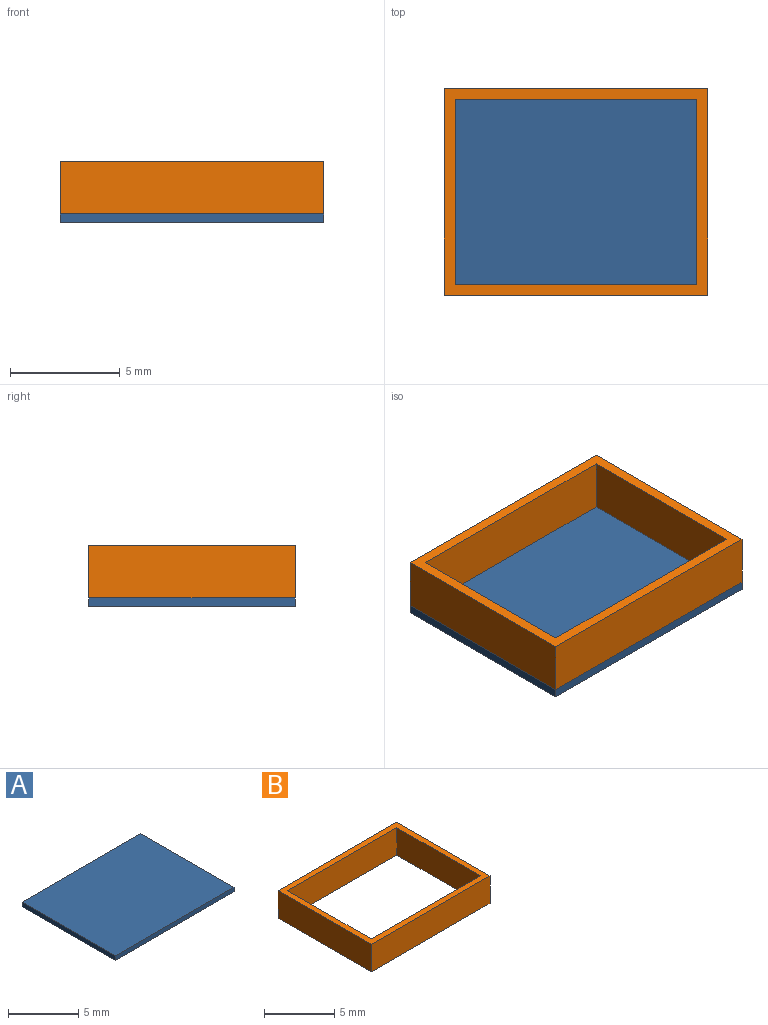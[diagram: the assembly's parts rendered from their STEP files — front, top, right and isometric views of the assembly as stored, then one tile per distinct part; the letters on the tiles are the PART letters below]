
ASSEMBLY  parts=2 mates=1
PART A: 6 faces, bbox 12x9.4x0.4 mm
  f0: plane 9.4x0.4mm, normal (-1,0,0), area 3.8mm2, adj f1,f3,f4,f5
  f1: plane 12x0.4mm, normal (0,-1,0), area 4.8mm2, adj f0,f2,f4,f5
  f2: plane 9.4x0.4mm, normal (1,0,0), area 3.8mm2, adj f1,f3,f4,f5
  f3: plane 12x0.4mm, normal (0,1,0), area 4.8mm2, adj f0,f2,f4,f5
  f4: plane 12x9.4mm, normal (0,0,-1), area 112.8mm2, adj f0,f1,f2,f3
  f5: plane 12x9.4mm, normal (0,0,1), area 112.8mm2, adj f0,f1,f2,f3
PART B: 10 faces, bbox 12x9.4x2.4 mm
  f0: plane 8.42x2.4mm, normal (-1,0,0), area 20.2mm2, adj f1,f7,f8,f9
  f1: plane 11.02x2.4mm, normal (0,1,0), area 26.4mm2, adj f0,f2,f8,f9
  f2: plane 8.42x2.4mm, normal (1,0,0), area 20.2mm2, adj f1,f7,f8,f9
  f3: plane 9.4x2.4mm, normal (-1,0,0), area 22.6mm2, adj f4,f6,f8,f9
  f4: plane 12x2.4mm, normal (0,-1,0), area 28.8mm2, adj f3,f5,f8,f9
  f5: plane 9.4x2.4mm, normal (1,0,0), area 22.6mm2, adj f4,f6,f8,f9
  f6: plane 12x2.4mm, normal (0,1,0), area 28.8mm2, adj f3,f5,f8,f9
  f7: plane 11.02x2.4mm, normal (0,-1,0), area 26.4mm2, adj f0,f2,f8,f9
  f8: plane 12x9.4mm, normal (0,0,1), area 20mm2, adj f0,f1,f2,f3,f4,f5,f6,f7
  f9: plane 12x9.4mm, normal (0,0,-1), area 20mm2, adj f0,f1,f2,f3,f4,f5,f6,f7
PLACE A t=(3.06,-16.32,-4.75)mm
PLACE B t=(3.06,-16.32,-4.75)mm
MATE planar B.f9 <-> A.f5  axis (0,0,-1) through (15.06,-6.92,-4.75)mm
